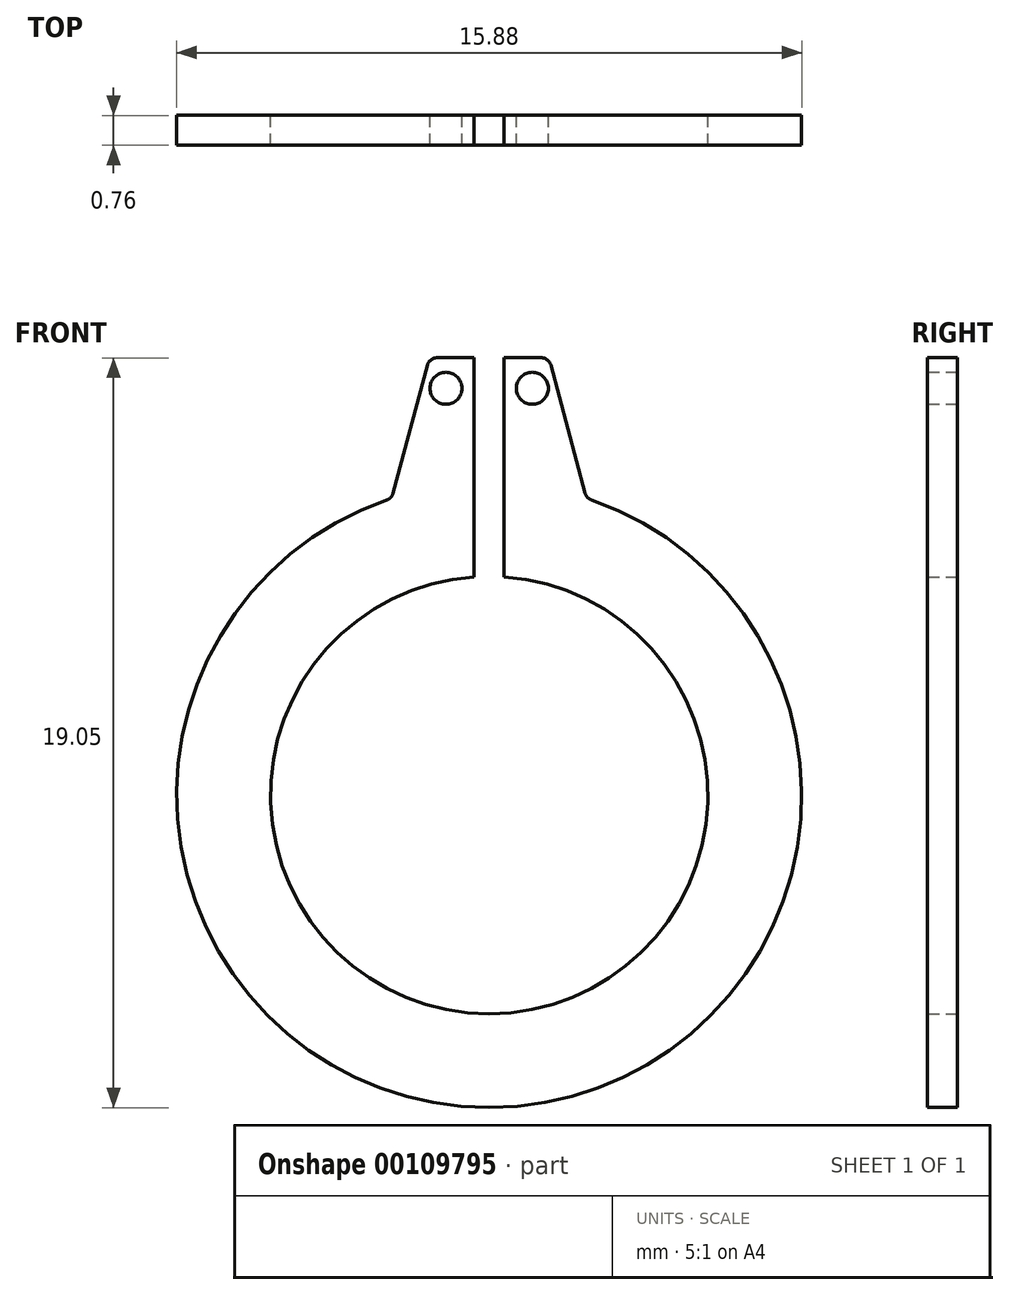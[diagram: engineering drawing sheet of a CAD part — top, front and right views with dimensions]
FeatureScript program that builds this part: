
annotation { "Feature Type Name" : "Feature", "Feature Type Description" : "" }
export const myFeature = defineFeature(function(context is Context, id is Id, definition is map)
    precondition{}
    {
        {
            var Q0;
            Q0=qCreatedBy(makeId("Front.planeOp"),FACE);
            var sketch = newSketch(context, id + "F0", { "sketchPlane" : qUnion([Q0])});
            skArc(sketch, "E0", {"start": v(-0.38, 5.54) * mm, "mid": v(0, -5.56) * mm, "end": v(0.38, 5.54) * mm});
            skArc(sketch, "E1", {"start": v(-2.48, 7.54) * mm, "mid": v(0, -7.94) * mm, "end": v(2.48, 7.54) * mm});
            skLineSegment(sketch, "E2.bottom", {"start": v(-1.52, 11.11) * mm, "end": v(-0.38, 11.11) * mm});
            skLineSegment(sketch, "E2.right", {"start": v(-0.38, 11.11) * mm, "end": v(-0.38, 5.54) * mm});
            skLineSegment(sketch, "E3", {"start": v(-1.52, 11.11) * mm, "end": v(-2.48, 7.54) * mm});
            skLineSegment(sketch, "E4.MirrorCS", {"start": v(1.52, 11.11) * mm, "end": v(2.48, 7.54) * mm});
            skLineSegment(sketch, "E5.MirrorCS", {"start": v(0.38, 11.11) * mm, "end": v(0.38, 5.54) * mm});
            skLineSegment(sketch, "E6.MirrorCS", {"start": v(1.52, 11.11) * mm, "end": v(0.38, 11.11) * mm});
            skPoint(sketch, "E7.orphan", {"position": v(-0.38, 7.93) * mm});
            skPoint(sketch, "E8.orphan", {"position": v(0.38, 7.93) * mm});
            skCircle(sketch, "E9", {"center": v(-1.1, 10.34) * mm, "radius": 0.4 * mm});
            skCircle(sketch, "E10.MirrorC", {"center": v(1.1, 10.34) * mm, "radius": 0.4 * mm});
            skSolve(sketch);
        }
        {
            var Q0;
            Q0 = qSketchRegion(id + "F0", true);
            extrude(context, id + "F1", {"entities" : qUnion([Q0]), "endBound" : BoundingType.SYMMETRIC, "depth" : 0.76 * mm});
        }
        {
            var Q0;
            Q0=makeQuery(id+"F1.opExtrude","SWEPT_EDGE",EDGE,{"disambiguationData":[OSD([sQuery(id+"F0.wireOp",EDGE,"E2.bottom"),sQuery(id+"F0.wireOp",EDGE,"E3")])]});
            var Q1;
            Q1=makeQuery(id+"F1.opExtrude","SWEPT_EDGE",EDGE,{"disambiguationData":[OSD([sQuery(id+"F0.wireOp",EDGE,"E4.MirrorCS"),sQuery(id+"F0.wireOp",EDGE,"E6.MirrorCS")])]});
            var Q2;
            Q2=makeQuery(id+"F1.opExtrude","SWEPT_EDGE",EDGE,{"disambiguationData":[OSD([sQuery(id+"F0.wireOp",EDGE,"E1"),sQuery(id+"F0.wireOp",EDGE,"E3")])]});
            var Q3;
            Q3=makeQuery(id+"F1.opExtrude","SWEPT_EDGE",EDGE,{"disambiguationData":[OSD([sQuery(id+"F0.wireOp",EDGE,"E1"),sQuery(id+"F0.wireOp",EDGE,"E4.MirrorCS")])]});
            fillet(context, id + "F2", {"entities" : qUnion([Q0, Q1, Q2, Q3]), "radius" : 0.25 * mm, "tangentPropagation" : true, "allowEdgeOverflow" : false});
        }
    });
